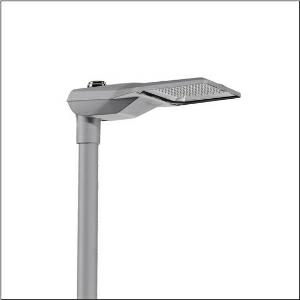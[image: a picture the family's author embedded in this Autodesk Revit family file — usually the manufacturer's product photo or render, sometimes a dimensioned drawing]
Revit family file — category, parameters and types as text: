
# Revit family: streetlight_sl_21_midi___st1_0a_5xe7d47n08lb_f0d9
name_source: partatom
category: Lighting Fixtures
units: mm (PartAtom-declared; Revit-internal decimal feet)

## family parameters
Cut with Voids When Loaded = No
Host = Face
Light Source = No
Part Type = Normal
Room Calculation Point = No
Round Connector Dimension = Use Diameter
Shared = No

## types (1)
- --- (1 x LED, 14950 lm, 98.3 W, 4000K)
    Apparent Load = 98 VA
    CIE Flux Codes = 37 72 97 100 100
    Color Rendering = 70
    Color Temperature = 4000K
    Default Elevation = 1800 mm
    Description = Streetlight SL 21 midi, mast luminaire, primary light control with lens, of PMMA, primary optical cover: cover, of toughened safety glass, transparent, light distribution: ST1.0a, light emission: direct distribution, primary light characteristic: asymmetric, installation type: side-entry, LED, 3G 2.5mm², High Power LED, rated luminous flux: 14.950lm, luminous efficacy: 152lm/W, light colour: 740, colour temperature: 4000K, control gear: NEMA (7pin), control: overheat protection, pre-setting: linear dimming characteristic, constant luminous flux control, time-dependent luminous flux control, flexible luminous flux parameterisation, mains connection: 220..240V, AC, 50/60Hz, connection cable pre-assembled, cable length: 10,5m, wiring characteristics: H05VV-F, start of lifetime: 98W, end of service life: 101W, reduction: 45W, luminaire housing, of diecast aluminium (EN AC-44300), powder-coated, Siteco® metallic grey (DB 702S), corrosivity category C5 mid according to DIN EN ISO 12944, multi-level sealing system, sealing non-destructively replaceable, inclination adjustable: 0°, 5°, 10°, 15°, length: 644mm, width: 335mm, height: 110mm, spigot size: 42mm (side-entry), mounting height: 4..8m, protection rating (complete): IP66, insulation class (complete): insulation class I (protective earthing), certification: CE, ENEC, ENEC+, VDE, impact resistance: IK10, permissible operating ambient temperature for outdoor applications: -40..+50°C, standard-compliant lighting for roads and squares, packaging unit: 1 piece

Light Distribution: ST1.0a
    Height = 111 mm
    Lamp = 1 x LED
    Lamp Light Flux = 14950 lm
    Lamp Power = 98.3 W
    Lamp count = 1
    Length = 644 mm
    Luminous efficacy = 152 lm/W
    Manufacturer = Siteco
    ModVariant = No
    Model = 5XE7D47N08LB
    Number of Poles = 1
    OnlyDefault = Yes
    Power Factor = 1
    Product Name = Streetlight SL 21 midi | ST1.0a
    Product group = mast luminaire | pylon top
    ProductGroupID = 6100
    Protection Class = Protection class I
    Protection Degree = IP 66
    RLX_Detail_Level = 1
    RLX_Emergency_Light_Flux = 0 lm
    RLX_Emergency_Type = 0
    RLX_Emergency_Type_DB = No
    RlxData = <blob elided: 26705 chars, md5=8bc3da58>
    Socket = socket
    Standby Power = 0 W
    System Light Flux = 14950 lm
    System Power = 98 W
    Type Comments = factory setting: luminous flux: 100 % | dim-lin: 254 | 1020 mA
    Type Image = l_1294377.jpg
    URL = http://relux.com
    VarID = @adj_136008
    Voltage = 0 V
    Weight = 0.00 kg
    Width = 336 mm

## geometry (parser evidence)
native form markers: Blend x4, Sweep x9
no freeform markers — native parametric forms only
